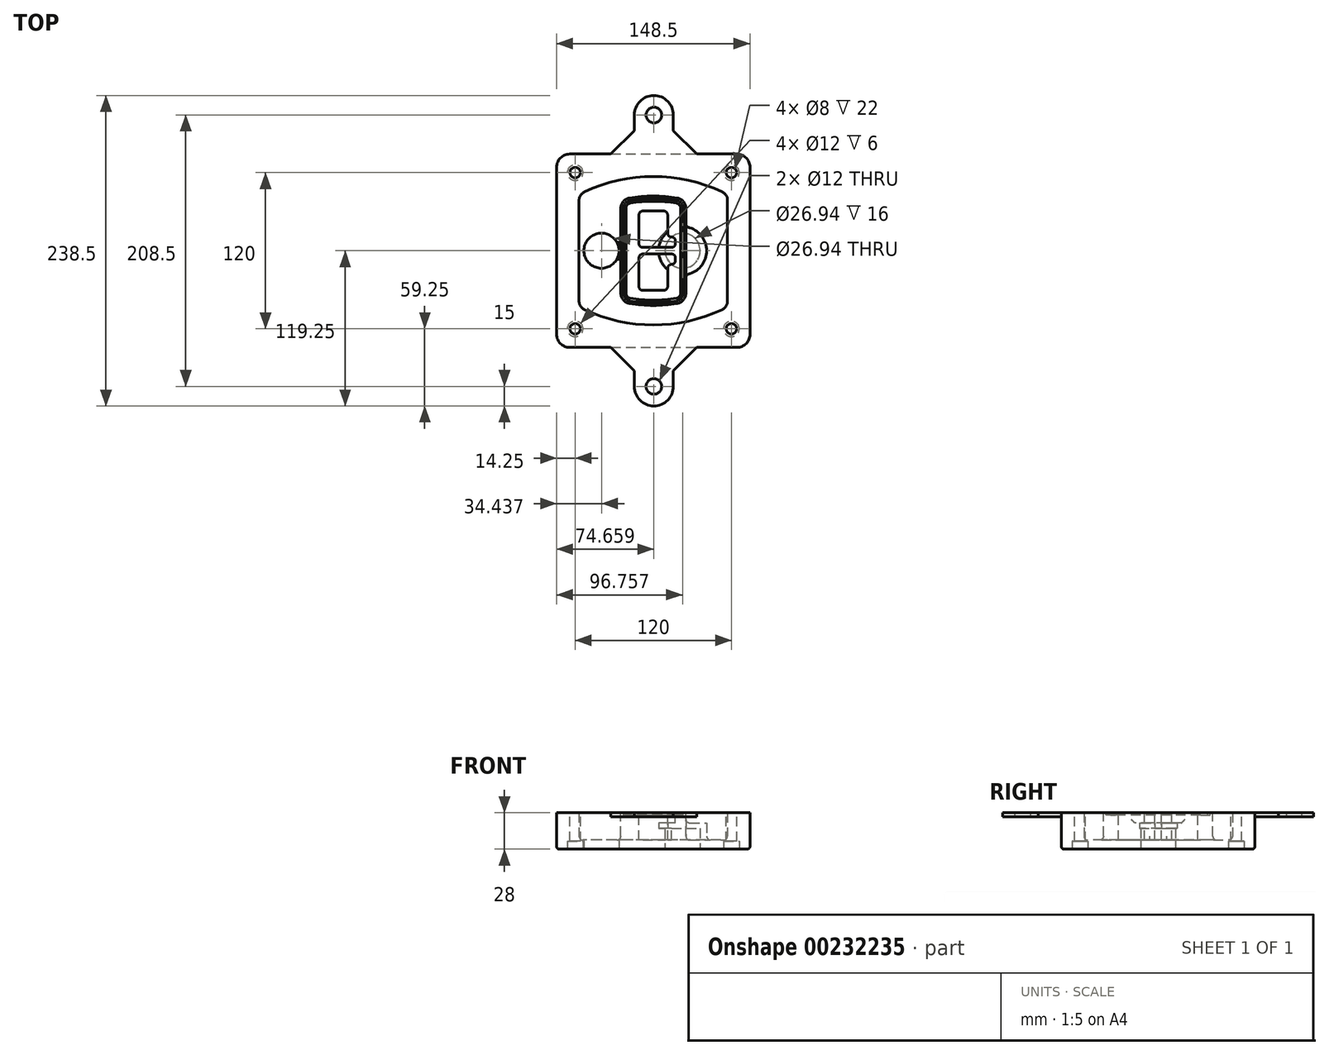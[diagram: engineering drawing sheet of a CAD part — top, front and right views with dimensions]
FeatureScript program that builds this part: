
annotation { "Feature Type Name" : "Feature", "Feature Type Description" : "" }
export const myFeature = defineFeature(function(context is Context, id is Id, definition is map)
    precondition{}
    {
        {
            var Q0;
            Q0=qCreatedBy(makeId("Top.planeOp"),FACE);
            var sketch = newSketch(context, id + "F0", { "sketchPlane" : qUnion([Q0])});
            skPoint(sketch, "E0.rect.middle", {"position": v(0, 0) * mm});
            skLineSegment(sketch, "E1.bottom", {"start": v(-64.25, -74.25) * mm, "end": v(64.25, -74.25) * mm});
            skLineSegment(sketch, "E1.top", {"start": v(-64.25, 74.25) * mm, "end": v(64.25, 74.25) * mm});
            skLineSegment(sketch, "E1.left", {"start": v(-74.25, -64.25) * mm, "end": v(-74.25, 64.25) * mm});
            skLineSegment(sketch, "E1.right", {"start": v(74.25, -64.25) * mm, "end": v(74.25, 64.25) * mm});
            skLineSegment(sketch, "E2", {"start": v(-74.25, 74.25) * mm, "end": v(74.25, -74.25) * mm, "construction": true});
            skLineSegment(sketch, "E3", {"start": v(74.25, 74.25) * mm, "end": v(-74.25, -74.25) * mm, "construction": true});
            skCircle(sketch, "E4", {"center": v(-60, 60) * mm, "radius": 4 * mm});
            skCircle(sketch, "E5", {"center": v(60, 60) * mm, "radius": 4 * mm});
            skCircle(sketch, "E6", {"center": v(60, -60) * mm, "radius": 4 * mm});
            skCircle(sketch, "E7", {"center": v(-60, -60) * mm, "radius": 4 * mm});
            skLineSegment(sketch, "E8", {"start": v(-60, 60) * mm, "end": v(60, 60) * mm, "construction": true});
            skLineSegment(sketch, "E9", {"start": v(60, 60) * mm, "end": v(60, -60) * mm, "construction": true});
            skLineSegment(sketch, "E10", {"start": v(60, -60) * mm, "end": v(-60, -60) * mm, "construction": true});
            skLineSegment(sketch, "E11", {"start": v(-60, -60) * mm, "end": v(-60, 60) * mm, "construction": true});
            skLineSegment(sketch, "E12", {"start": v(-60, 38.83) * mm, "end": v(-60, -38.83) * mm});
            skLineSegment(sketch, "E13", {"start": v(60, 38.83) * mm, "end": v(60, -38.83) * mm});
            skArc(sketch, "E14", {"start": v(54.26, 47.88) * mm, "mid": v(0, 60) * mm, "end": v(-54.26, 47.88) * mm});
            skArc(sketch, "E15", {"start": v(-54.26, -47.88) * mm, "mid": v(0, -60) * mm, "end": v(54.26, -47.88) * mm});
            skLineSegment(sketch, "E16", {"start": v(-60, 0) * mm, "end": v(60, 0) * mm, "construction": true});
            skPoint(sketch, "E17.visualSharp", {"position": v(-60, -45) * mm});
            skArc(sketch, "E17.filletArc", {"start": v(-60, -38.83) * mm, "mid": v(-58.44, -44.2) * mm, "end": v(-54.26, -47.88) * mm});
            skPoint(sketch, "E18.visualSharp", {"position": v(-60, 45) * mm});
            skArc(sketch, "E18.filletArc", {"start": v(-54.26, 47.88) * mm, "mid": v(-58.44, 44.2) * mm, "end": v(-60, 38.83) * mm});
            skPoint(sketch, "E19.visualSharp", {"position": v(60, 45) * mm});
            skArc(sketch, "E19.filletArc", {"start": v(60, 38.83) * mm, "mid": v(58.44, 44.2) * mm, "end": v(54.26, 47.88) * mm});
            skPoint(sketch, "E20.visualSharp", {"position": v(60, -45) * mm});
            skArc(sketch, "E20.filletArc", {"start": v(54.26, -47.88) * mm, "mid": v(58.44, -44.2) * mm, "end": v(60, -38.83) * mm});
            skPoint(sketch, "E21.visualSharp", {"position": v(-74.25, 74.25) * mm});
            skArc(sketch, "E21.filletArc", {"start": v(-64.25, 74.25) * mm, "mid": v(-71.32, 71.32) * mm, "end": v(-74.25, 64.25) * mm});
            skPoint(sketch, "E22.visualSharp", {"position": v(74.25, 74.25) * mm});
            skArc(sketch, "E22.filletArc", {"start": v(74.25, 64.25) * mm, "mid": v(71.32, 71.32) * mm, "end": v(64.25, 74.25) * mm});
            skPoint(sketch, "E23.visualSharp", {"position": v(74.25, -74.25) * mm});
            skArc(sketch, "E23.filletArc", {"start": v(64.25, -74.25) * mm, "mid": v(71.32, -71.32) * mm, "end": v(74.25, -64.25) * mm});
            skPoint(sketch, "E24.visualSharp", {"position": v(-74.25, -74.25) * mm});
            skArc(sketch, "E24.filletArc", {"start": v(-74.25, -64.25) * mm, "mid": v(-71.32, -71.32) * mm, "end": v(-64.25, -74.25) * mm});
            skArc(sketch, "E25.0", {"start": v(57, 38.83) * mm, "mid": v(55.9, 42.58) * mm, "end": v(52.98, 45.17) * mm});
            skLineSegment(sketch, "E25.1", {"start": v(57, 38.83) * mm, "end": v(57, -38.83) * mm});
            skArc(sketch, "E25.2", {"start": v(52.98, -45.17) * mm, "mid": v(55.9, -42.58) * mm, "end": v(57, -38.83) * mm});
            skArc(sketch, "E25.3", {"start": v(-52.98, -45.17) * mm, "mid": v(0, -57) * mm, "end": v(52.98, -45.17) * mm});
            skArc(sketch, "E25.4", {"start": v(-57, -38.83) * mm, "mid": v(-55.9, -42.58) * mm, "end": v(-52.98, -45.17) * mm});
            skArc(sketch, "E25.5", {"start": v(52.98, 45.17) * mm, "mid": v(0, 57) * mm, "end": v(-52.98, 45.17) * mm});
            skLineSegment(sketch, "E25.6", {"start": v(-57, 38.83) * mm, "end": v(-57, -38.83) * mm});
            skArc(sketch, "E25.7", {"start": v(-52.98, 45.17) * mm, "mid": v(-55.9, 42.58) * mm, "end": v(-57, 38.83) * mm});
            skArc(sketch, "E26.0", {"start": v(-55.96, 51.5) * mm, "mid": v(-61.82, 46.33) * mm, "end": v(-64, 38.83) * mm});
            skArc(sketch, "E26.1", {"start": v(55.96, 51.5) * mm, "mid": v(0, 64) * mm, "end": v(-55.96, 51.5) * mm});
            skArc(sketch, "E26.2", {"start": v(64, 38.83) * mm, "mid": v(61.82, 46.33) * mm, "end": v(55.96, 51.5) * mm});
            skLineSegment(sketch, "E26.3", {"start": v(64, 38.83) * mm, "end": v(64, -38.83) * mm});
            skArc(sketch, "E26.4", {"start": v(55.96, -51.5) * mm, "mid": v(61.82, -46.33) * mm, "end": v(64, -38.83) * mm});
            skLineSegment(sketch, "E26.5", {"start": v(-64, 38.83) * mm, "end": v(-64, -38.83) * mm});
            skArc(sketch, "E26.6", {"start": v(-55.96, -51.5) * mm, "mid": v(0, -64) * mm, "end": v(55.96, -51.5) * mm});
            skArc(sketch, "E26.7", {"start": v(-64, -38.83) * mm, "mid": v(-61.82, -46.33) * mm, "end": v(-55.96, -51.5) * mm});
            skSolve(sketch);
        }
        {
            var Q0;
            Q0=makeQuery(id+"F0.imprint","IMPRINT",FACE,{"disambiguationData":[TD([[makeQuery(id+"F0.imprint","IMPRINT",EDGE,{"derivedFrom":sQuery(id+"F0.wireOp",EDGE,"E1.bottom")}),1.0]])]});
            var Q1;
            Q1=makeQuery(id+"F0.imprint","IMPRINT",FACE,{"disambiguationData":[TD([[makeQuery(id+"F0.imprint","IMPRINT",EDGE,{"derivedFrom":sQuery(id+"F0.wireOp",EDGE,"E12")}),1.0]])]});
            var Q2;
            Q2=makeQuery(id+"F0.imprint","IMPRINT",FACE,{"disambiguationData":[TD([[makeQuery(id+"F0.imprint","IMPRINT",EDGE,{"derivedFrom":sQuery(id+"F0.wireOp",EDGE,"E25.0")}),1.0]])]});
            var Q3;
            Q3=makeQuery(id+"F0.imprint","IMPRINT",FACE,{"disambiguationData":[TD([[makeQuery(id+"F0.imprint","IMPRINT",EDGE,{"derivedFrom":sQuery(id+"F0.wireOp",EDGE,"E12")}),-1.0]])]});
            extrude(context, id + "F1", {"entities" : qUnion([Q0, Q1, Q2, Q3]), "oppositeDirection" : true, "depth" : 25 * mm});
        }
        {
            var Q0;
            Q0=makeQuery(id+"F0.imprint","IMPRINT",FACE,{"disambiguationData":[TD([[makeQuery(id+"F0.imprint","IMPRINT",EDGE,{"derivedFrom":sQuery(id+"F0.wireOp",EDGE,"E12")}),1.0]])]});
            extrude(context, id + "F2", {"entities" : qUnion([Q0]), "operationType" : NewBodyOperationType.ADD, "depth" : 3 * mm});
        }
        {
            var Q0;
            Q0=makeQuery(id+"F0.imprint","IMPRINT",FACE,{"disambiguationData":[TD([[makeQuery(id+"F0.imprint","IMPRINT",EDGE,{"derivedFrom":sQuery(id+"F0.wireOp",EDGE,"E25.0")}),1.0]])]});
            extrude(context, id + "F3", {"entities" : qUnion([Q0]), "operationType" : NewBodyOperationType.REMOVE, "oppositeDirection" : true, "depth" : 18 * mm});
        }
        {
            var Q0;
            Q0=makeQuery(id+"F2.opExtrude","CAP_FACE",FACE,{"disambiguationData":[OSD([sQuery(id+"F0.wireOp",EDGE,"E12"),sQuery(id+"F0.wireOp",EDGE,"E13"),sQuery(id+"F0.wireOp",EDGE,"E14"),sQuery(id+"F0.wireOp",EDGE,"E15"),sQuery(id+"F0.wireOp",EDGE,"E17.filletArc"),sQuery(id+"F0.wireOp",EDGE,"E18.filletArc"),sQuery(id+"F0.wireOp",EDGE,"E19.filletArc"),sQuery(id+"F0.wireOp",EDGE,"E20.filletArc"),sQuery(id+"F0.wireOp",EDGE,"E25.0"),sQuery(id+"F0.wireOp",EDGE,"E25.1"),sQuery(id+"F0.wireOp",EDGE,"E25.2"),sQuery(id+"F0.wireOp",EDGE,"E25.3"),sQuery(id+"F0.wireOp",EDGE,"E25.4"),sQuery(id+"F0.wireOp",EDGE,"E25.5"),sQuery(id+"F0.wireOp",EDGE,"E25.6"),sQuery(id+"F0.wireOp",EDGE,"E25.7")])],"isStart":false});
            var sketch = newSketch(context, id + "F4", { "sketchPlane" : qUnion([Q0])});
            skArc(sketch, "E27.0", {"start": v(-18.34, -40.45) * mm, "mid": v(0, -42) * mm, "end": v(18.34, -40.45) * mm});
            skArc(sketch, "E28.0", {"start": v(18.34, 40.45) * mm, "mid": v(0, 42) * mm, "end": v(-18.34, 40.45) * mm});
            skLineSegment(sketch, "E29", {"start": v(-25, 32.57) * mm, "end": v(-25, -32.57) * mm});
            skLineSegment(sketch, "E30", {"start": v(25, 32.57) * mm, "end": v(25, -32.57) * mm});
            skLineSegment(sketch, "E31", {"start": v(-25, 39.1) * mm, "end": v(25, 39.1) * mm, "construction": true});
            skLineSegment(sketch, "E32", {"start": v(-25, -39.1) * mm, "end": v(25, -39.1) * mm, "construction": true});
            skPoint(sketch, "E33.visualSharp", {"position": v(-25, 39.1) * mm});
            skArc(sketch, "E33.filletArc", {"start": v(-18.34, 40.45) * mm, "mid": v(-23.11, 37.73) * mm, "end": v(-25, 32.57) * mm});
            skPoint(sketch, "E34.visualSharp", {"position": v(25, 39.1) * mm});
            skArc(sketch, "E34.filletArc", {"start": v(25, 32.57) * mm, "mid": v(23.11, 37.73) * mm, "end": v(18.34, 40.45) * mm});
            skPoint(sketch, "E35.visualSharp", {"position": v(25, -39.1) * mm});
            skArc(sketch, "E35.filletArc", {"start": v(18.34, -40.45) * mm, "mid": v(23.11, -37.73) * mm, "end": v(25, -32.57) * mm});
            skPoint(sketch, "E36.visualSharp", {"position": v(-25, -39.1) * mm});
            skArc(sketch, "E36.filletArc", {"start": v(-25, -32.57) * mm, "mid": v(-23.11, -37.73) * mm, "end": v(-18.34, -40.45) * mm});
            skArc(sketch, "E37.0", {"start": v(52.98, 45.17) * mm, "mid": v(0, 57) * mm, "end": v(-52.98, 45.17) * mm});
            skArc(sketch, "E37.1", {"start": v(-52.98, 45.17) * mm, "mid": v(-55.9, 42.58) * mm, "end": v(-57, 38.83) * mm});
            skLineSegment(sketch, "E37.2", {"start": v(-57, 38.83) * mm, "end": v(-57, -38.83) * mm});
            skArc(sketch, "E37.3", {"start": v(-57, -38.83) * mm, "mid": v(-55.9, -42.58) * mm, "end": v(-52.98, -45.17) * mm});
            skArc(sketch, "E37.4", {"start": v(-52.98, -45.17) * mm, "mid": v(0, -57) * mm, "end": v(52.98, -45.17) * mm});
            skArc(sketch, "E37.5", {"start": v(52.98, -45.17) * mm, "mid": v(55.9, -42.58) * mm, "end": v(57, -38.83) * mm});
            skLineSegment(sketch, "E37.6", {"start": v(57, 38.83) * mm, "end": v(57, -38.83) * mm});
            skArc(sketch, "E37.7", {"start": v(57, 38.83) * mm, "mid": v(55.9, 42.58) * mm, "end": v(52.98, 45.17) * mm});
            skLineSegment(sketch, "E38.0", {"start": v(23, 32.57) * mm, "end": v(23, -32.57) * mm});
            skArc(sketch, "E38.1", {"start": v(18, -38.48) * mm, "mid": v(21.58, -36.44) * mm, "end": v(23, -32.57) * mm});
            skArc(sketch, "E38.2", {"start": v(-18, -38.48) * mm, "mid": v(0, -40) * mm, "end": v(18, -38.48) * mm});
            skArc(sketch, "E38.3", {"start": v(-23, -32.57) * mm, "mid": v(-21.58, -36.44) * mm, "end": v(-18, -38.48) * mm});
            skLineSegment(sketch, "E38.4", {"start": v(-23, 32.57) * mm, "end": v(-23, -32.57) * mm});
            skArc(sketch, "E38.5", {"start": v(23, 32.57) * mm, "mid": v(21.58, 36.44) * mm, "end": v(18, 38.48) * mm});
            skArc(sketch, "E38.6", {"start": v(-18, 38.48) * mm, "mid": v(-21.58, 36.44) * mm, "end": v(-23, 32.57) * mm});
            skArc(sketch, "E38.7", {"start": v(18, 38.48) * mm, "mid": v(0, 40) * mm, "end": v(-18, 38.48) * mm});
            skArc(sketch, "E39.0", {"start": v(21, 32.57) * mm, "mid": v(20.06, 35.15) * mm, "end": v(17.67, 36.5) * mm});
            skLineSegment(sketch, "E39.1", {"start": v(21, 32.57) * mm, "end": v(21, -32.57) * mm});
            skArc(sketch, "E39.2", {"start": v(17.67, -36.5) * mm, "mid": v(20.06, -35.15) * mm, "end": v(21, -32.57) * mm});
            skArc(sketch, "E39.3", {"start": v(-17.67, -36.5) * mm, "mid": v(0, -38) * mm, "end": v(17.67, -36.5) * mm});
            skArc(sketch, "E39.4", {"start": v(-21, -32.57) * mm, "mid": v(-20.06, -35.15) * mm, "end": v(-17.67, -36.5) * mm});
            skArc(sketch, "E39.5", {"start": v(17.67, 36.5) * mm, "mid": v(0, 38) * mm, "end": v(-17.67, 36.5) * mm});
            skLineSegment(sketch, "E39.6", {"start": v(-21, 32.57) * mm, "end": v(-21, -32.57) * mm});
            skArc(sketch, "E39.7", {"start": v(-17.67, 36.5) * mm, "mid": v(-20.06, 35.15) * mm, "end": v(-21, 32.57) * mm});
            skLineSegment(sketch, "E40", {"start": v(-25, 0) * mm, "end": v(25, 0) * mm, "construction": true});
            skLineSegment(sketch, "E41", {"start": v(-11, 5.5) * mm, "end": v(-11, 27.5) * mm});
            skLineSegment(sketch, "E42", {"start": v(-8, 30.5) * mm, "end": v(8, 30.5) * mm});
            skLineSegment(sketch, "E43", {"start": v(11, 27.5) * mm, "end": v(11, 13.5) * mm});
            skLineSegment(sketch, "E44", {"start": v(14, 10.5) * mm, "end": v(14, 10.5) * mm});
            skLineSegment(sketch, "E45", {"start": v(17, 7.5) * mm, "end": v(17, 5.5) * mm});
            skLineSegment(sketch, "E46", {"start": v(14, 2.5) * mm, "end": v(-8, 2.5) * mm});
            skPoint(sketch, "E47.visualSharp", {"position": v(-11, 30.5) * mm});
            skArc(sketch, "E47.filletArc", {"start": v(-8, 30.5) * mm, "mid": v(-10.12, 29.62) * mm, "end": v(-11, 27.5) * mm});
            skPoint(sketch, "E48.visualSharp", {"position": v(11, 30.5) * mm});
            skArc(sketch, "E48.filletArc", {"start": v(11, 27.5) * mm, "mid": v(10.12, 29.62) * mm, "end": v(8, 30.5) * mm});
            skPoint(sketch, "E49.visualSharp", {"position": v(11, 10.5) * mm});
            skArc(sketch, "E49.filletArc", {"start": v(11, 13.5) * mm, "mid": v(11.88, 11.38) * mm, "end": v(14, 10.5) * mm});
            skPoint(sketch, "E50.visualSharp", {"position": v(17, 10.5) * mm});
            skArc(sketch, "E50.filletArc", {"start": v(17, 7.5) * mm, "mid": v(16.12, 9.62) * mm, "end": v(14, 10.5) * mm});
            skPoint(sketch, "E51.visualSharp", {"position": v(17, 2.5) * mm});
            skArc(sketch, "E51.filletArc", {"start": v(14, 2.5) * mm, "mid": v(16.12, 3.38) * mm, "end": v(17, 5.5) * mm});
            skPoint(sketch, "E52.visualSharp", {"position": v(-11, 2.5) * mm});
            skArc(sketch, "E52.filletArc", {"start": v(-11, 5.5) * mm, "mid": v(-10.12, 3.38) * mm, "end": v(-8, 2.5) * mm});
            skLineSegment(sketch, "E53.0.MirrorCS", {"start": v(14, -2.5) * mm, "end": v(-8, -2.5) * mm});
            skArc(sketch, "E54.0.MirrorCS", {"start": v(-11, -5.5) * mm, "mid": v(-10.12, -3.38) * mm, "end": v(-8, -2.5) * mm});
            skLineSegment(sketch, "E55.0.MirrorCS", {"start": v(-11, -5.5) * mm, "end": v(-11, -27.5) * mm});
            skArc(sketch, "E56.0.MirrorCS", {"start": v(-8, -30.5) * mm, "mid": v(-10.12, -29.62) * mm, "end": v(-11, -27.5) * mm});
            skLineSegment(sketch, "E57.0.MirrorCS", {"start": v(-8, -30.5) * mm, "end": v(8, -30.5) * mm});
            skArc(sketch, "E58.0.MirrorCS", {"start": v(11, -27.5) * mm, "mid": v(10.12, -29.62) * mm, "end": v(8, -30.5) * mm});
            skLineSegment(sketch, "E59.0.MirrorCS", {"start": v(11, -27.5) * mm, "end": v(11, -13.5) * mm});
            skArc(sketch, "E60.0.MirrorCS", {"start": v(11, -13.5) * mm, "mid": v(11.88, -11.38) * mm, "end": v(14, -10.5) * mm});
            skArc(sketch, "E61.0.MirrorCS", {"start": v(17, -7.5) * mm, "mid": v(16.12, -9.62) * mm, "end": v(14, -10.5) * mm});
            skLineSegment(sketch, "E62.0.MirrorCS", {"start": v(17, -7.5) * mm, "end": v(17, -5.5) * mm});
            skArc(sketch, "E63.0.MirrorCS", {"start": v(14, -2.5) * mm, "mid": v(16.12, -3.38) * mm, "end": v(17, -5.5) * mm});
            skSolve(sketch);
        }
        {
            var Q0;
            Q0=makeQuery(id+"F4.imprint","IMPRINT",FACE,{"disambiguationData":[TD([[makeQuery(id+"F4.imprint","IMPRINT",EDGE,{"derivedFrom":sQuery(id+"F4.wireOp",EDGE,"E27.0")}),1.0]])]});
            var Q1;
            Q1=makeQuery(id+"F4.imprint","IMPRINT",FACE,{"disambiguationData":[TD([[makeQuery(id+"F4.imprint","IMPRINT",EDGE,{"derivedFrom":sQuery(id+"F4.wireOp",EDGE,"E38.0")}),-1.0]])]});
            var Q2;
            Q2=makeQuery(id+"F4.imprint","IMPRINT",FACE,{"disambiguationData":[TD([[makeQuery(id+"F4.imprint","IMPRINT",EDGE,{"derivedFrom":sQuery(id+"F4.wireOp",EDGE,"E39.0")}),1.0]])]});
            extrude(context, id + "F5", {"entities" : qUnion([Q0, Q1, Q2]), "operationType" : NewBodyOperationType.ADD, "endBound" : BoundingType.UP_TO_NEXT, "oppositeDirection" : true, "depth" : 25 * mm});
        }
        {
            var Q0;
            Q0=makeQuery(id+"F4.imprint","IMPRINT",FACE,{"disambiguationData":[TD([[makeQuery(id+"F4.imprint","IMPRINT",EDGE,{"derivedFrom":sQuery(id+"F4.wireOp",EDGE,"E38.0")}),-1.0]])]});
            extrude(context, id + "F6", {"entities" : qUnion([Q0]), "operationType" : NewBodyOperationType.REMOVE, "oppositeDirection" : true, "depth" : 2 * mm});
        }
        {
            var Q0;
            Q0=makeQuery(id+"F1.opExtrude","CAP_FACE",FACE,{"disambiguationData":[OSD([sQuery(id+"F0.wireOp",EDGE,"E1.bottom"),sQuery(id+"F0.wireOp",EDGE,"E1.top"),sQuery(id+"F0.wireOp",EDGE,"E1.left"),sQuery(id+"F0.wireOp",EDGE,"E1.right"),sQuery(id+"F0.wireOp",EDGE,"E4"),sQuery(id+"F0.wireOp",EDGE,"E5"),sQuery(id+"F0.wireOp",EDGE,"E6"),sQuery(id+"F0.wireOp",EDGE,"E7"),sQuery(id+"F0.wireOp",EDGE,"E21.filletArc"),sQuery(id+"F0.wireOp",EDGE,"E22.filletArc"),sQuery(id+"F0.wireOp",EDGE,"E23.filletArc"),sQuery(id+"F0.wireOp",EDGE,"E24.filletArc")])],"isStart":false});
            var sketch = newSketch(context, id + "F7", { "sketchPlane" : qUnion([Q0])});
            skCircle(sketch, "E64", {"center": v(22.5, 0) * mm, "radius": 13.47 * mm});
            skCircle(sketch, "E65", {"center": v(-39.81, 0) * mm, "radius": 13.47 * mm});
            skLineSegment(sketch, "E66", {"start": v(74.25, 0) * mm, "end": v(-74.25, 0) * mm});
            skCircle(sketch, "E67", {"center": v(22.5, 0) * mm, "radius": 18.47 * mm});
            skCircle(sketch, "E68", {"center": v(60, -60) * mm, "radius": 6 * mm});
            skCircle(sketch, "E69", {"center": v(-60, -60) * mm, "radius": 6 * mm});
            skCircle(sketch, "E70", {"center": v(-60, 60) * mm, "radius": 6 * mm});
            skCircle(sketch, "E71", {"center": v(60, 60) * mm, "radius": 6 * mm});
            skSolve(sketch);
        }
        {
            var Q0;
            {var subQ1=sQuery(id+"F7.wireOp",EDGE,"E66");var subQ4=sQuery(id+"F7.wireOp",EDGE,"E64");var subQ6=makeQuery(id+"F7.imprint","INTERSECT",VERTEX,{"disambiguationData":[OD(0.0)],"derivedFrom":[subQ4,subQ1]});Q0=makeQuery(id+"F7.imprint","IMPRINT",FACE,{"disambiguationData":[TD([[makeQuery(id+"F7.imprint","IMPRINT",EDGE,{"disambiguationData":[TD([[subQ6,-1.0]])],"derivedFrom":subQ4}),-1.0]])]});}
            var Q1;
            {var subQ0=sQuery(id+"F7.wireOp",EDGE,"E66");var subQ1=sQuery(id+"F7.wireOp",EDGE,"E64");var subQ3=makeQuery(id+"F7.imprint","INTERSECT",VERTEX,{"disambiguationData":[OD(0.0)],"derivedFrom":[subQ1,subQ0]});Q1=makeQuery(id+"F7.imprint","IMPRINT",FACE,{"disambiguationData":[TD([[makeQuery(id+"F7.imprint","IMPRINT",EDGE,{"disambiguationData":[TD([[subQ3,-1.0]])],"derivedFrom":subQ1}),1.0]])]});}
            var Q2;
            {var subQ0=sQuery(id+"F7.wireOp",EDGE,"E66");var subQ1=sQuery(id+"F7.wireOp",EDGE,"E64");var subQ3=makeQuery(id+"F7.imprint","INTERSECT",VERTEX,{"disambiguationData":[OD(0.0)],"derivedFrom":[subQ1,subQ0]});Q2=makeQuery(id+"F7.imprint","IMPRINT",FACE,{"disambiguationData":[TD([[makeQuery(id+"F7.imprint","IMPRINT",EDGE,{"disambiguationData":[TD([[subQ3,1.0]])],"derivedFrom":subQ1}),1.0]])]});}
            var Q3;
            {var subQ1=sQuery(id+"F7.wireOp",EDGE,"E66");var subQ4=sQuery(id+"F7.wireOp",EDGE,"E64");var subQ6=makeQuery(id+"F7.imprint","INTERSECT",VERTEX,{"disambiguationData":[OD(0.0)],"derivedFrom":[subQ4,subQ1]});Q3=makeQuery(id+"F7.imprint","IMPRINT",FACE,{"disambiguationData":[TD([[makeQuery(id+"F7.imprint","IMPRINT",EDGE,{"disambiguationData":[TD([[subQ6,1.0]])],"derivedFrom":subQ4}),-1.0]])]});}
            extrude(context, id + "F8", {"entities" : qUnion([Q0, Q1, Q2, Q3]), "operationType" : NewBodyOperationType.ADD, "oppositeDirection" : true, "depth" : 20 * mm});
        }
        {
            var Q0;
            {var subQ0=sQuery(id+"F7.wireOp",EDGE,"E66");var subQ1=sQuery(id+"F7.wireOp",EDGE,"E64");var subQ3=makeQuery(id+"F7.imprint","INTERSECT",VERTEX,{"disambiguationData":[OD(0.0)],"derivedFrom":[subQ1,subQ0]});Q0=makeQuery(id+"F7.imprint","IMPRINT",FACE,{"disambiguationData":[TD([[makeQuery(id+"F7.imprint","IMPRINT",EDGE,{"disambiguationData":[TD([[subQ3,-1.0]])],"derivedFrom":subQ1}),1.0]])]});}
            var Q1;
            {var subQ0=sQuery(id+"F7.wireOp",EDGE,"E66");var subQ1=sQuery(id+"F7.wireOp",EDGE,"E64");var subQ3=makeQuery(id+"F7.imprint","INTERSECT",VERTEX,{"disambiguationData":[OD(0.0)],"derivedFrom":[subQ1,subQ0]});Q1=makeQuery(id+"F7.imprint","IMPRINT",FACE,{"disambiguationData":[TD([[makeQuery(id+"F7.imprint","IMPRINT",EDGE,{"disambiguationData":[TD([[subQ3,1.0]])],"derivedFrom":subQ1}),1.0]])]});}
            extrude(context, id + "F9", {"entities" : qUnion([Q0, Q1]), "operationType" : NewBodyOperationType.REMOVE, "oppositeDirection" : true, "depth" : 16 * mm});
        }
        {
            var Q0;
            {var subQ0=sQuery(id+"F7.wireOp",EDGE,"E66");var subQ1=sQuery(id+"F7.wireOp",EDGE,"E65");var subQ3=makeQuery(id+"F7.imprint","INTERSECT",VERTEX,{"disambiguationData":[OD(0.0)],"derivedFrom":[subQ1,subQ0]});Q0=makeQuery(id+"F7.imprint","IMPRINT",FACE,{"disambiguationData":[TD([[makeQuery(id+"F7.imprint","IMPRINT",EDGE,{"disambiguationData":[TD([[subQ3,-1.0]])],"derivedFrom":subQ1}),1.0]])]});}
            var Q1;
            {var subQ0=sQuery(id+"F7.wireOp",EDGE,"E66");var subQ1=sQuery(id+"F7.wireOp",EDGE,"E65");var subQ3=makeQuery(id+"F7.imprint","INTERSECT",VERTEX,{"disambiguationData":[OD(0.0)],"derivedFrom":[subQ1,subQ0]});Q1=makeQuery(id+"F7.imprint","IMPRINT",FACE,{"disambiguationData":[TD([[makeQuery(id+"F7.imprint","IMPRINT",EDGE,{"disambiguationData":[TD([[subQ3,1.0]])],"derivedFrom":subQ1}),1.0]])]});}
            extrude(context, id + "F10", {"entities" : qUnion([Q0, Q1]), "operationType" : NewBodyOperationType.REMOVE, "oppositeDirection" : true, "depth" : 25 * mm});
        }
        {
            var Q0;
            Q0=makeQuery(id+"F7.imprint","IMPRINT",FACE,{"disambiguationData":[TD([[makeQuery(id+"F7.imprint","IMPRINT",EDGE,{"derivedFrom":sQuery(id+"F7.wireOp",EDGE,"E68")}),1.0]])]});
            var Q1;
            Q1=makeQuery(id+"F7.imprint","IMPRINT",FACE,{"disambiguationData":[TD([[makeQuery(id+"F7.imprint","IMPRINT",EDGE,{"derivedFrom":makeQuery(id+"F1.opExtrude","CAP_EDGE",EDGE,{"disambiguationData":[OSD([sQuery(id+"F0.wireOp",EDGE,"E5")])],"isStart":false})}),-1.0]])]});
            var Q2;
            Q2=makeQuery(id+"F7.imprint","IMPRINT",FACE,{"disambiguationData":[TD([[makeQuery(id+"F7.imprint","IMPRINT",EDGE,{"derivedFrom":sQuery(id+"F7.wireOp",EDGE,"E69")}),1.0]])]});
            var Q3;
            Q3=makeQuery(id+"F7.imprint","IMPRINT",FACE,{"disambiguationData":[TD([[makeQuery(id+"F7.imprint","IMPRINT",EDGE,{"derivedFrom":makeQuery(id+"F1.opExtrude","CAP_EDGE",EDGE,{"disambiguationData":[OSD([sQuery(id+"F0.wireOp",EDGE,"E4")])],"isStart":false})}),-1.0]])]});
            var Q4;
            Q4=makeQuery(id+"F7.imprint","IMPRINT",FACE,{"disambiguationData":[TD([[makeQuery(id+"F7.imprint","IMPRINT",EDGE,{"derivedFrom":sQuery(id+"F7.wireOp",EDGE,"E70")}),1.0]])]});
            var Q5;
            Q5=makeQuery(id+"F7.imprint","IMPRINT",FACE,{"disambiguationData":[TD([[makeQuery(id+"F7.imprint","IMPRINT",EDGE,{"derivedFrom":makeQuery(id+"F1.opExtrude","CAP_EDGE",EDGE,{"disambiguationData":[OSD([sQuery(id+"F0.wireOp",EDGE,"E7")])],"isStart":false})}),-1.0]])]});
            var Q6;
            Q6=makeQuery(id+"F7.imprint","IMPRINT",FACE,{"disambiguationData":[TD([[makeQuery(id+"F7.imprint","IMPRINT",EDGE,{"derivedFrom":sQuery(id+"F7.wireOp",EDGE,"E71")}),1.0]])]});
            var Q7;
            Q7=makeQuery(id+"F7.imprint","IMPRINT",FACE,{"disambiguationData":[TD([[makeQuery(id+"F7.imprint","IMPRINT",EDGE,{"derivedFrom":makeQuery(id+"F1.opExtrude","CAP_EDGE",EDGE,{"disambiguationData":[OSD([sQuery(id+"F0.wireOp",EDGE,"E6")])],"isStart":false})}),-1.0]])]});
            extrude(context, id + "F11", {"entities" : qUnion([Q0, Q1, Q2, Q3, Q4, Q5, Q6, Q7]), "operationType" : NewBodyOperationType.REMOVE, "oppositeDirection" : true, "depth" : 6 * mm});
        }
        {
            var Q0;
            Q0=makeQuery(id+"F9.boolean.opBoolean","COPY",FACE,{"derivedFrom":makeQuery(id+"F9.opExtrude","CAP_FACE",FACE,{"disambiguationData":[OSD([sQuery(id+"F7.wireOp",EDGE,"E64")])],"isStart":false})});
            var sketch = newSketch(context, id + "F12", { "sketchPlane" : qUnion([Q0])});
            skArc(sketch, "E72.0", {"start": v(11, 14.45) * mm, "mid": v(6.45, 9.13) * mm, "end": v(4.2, 2.5) * mm});
            skArc(sketch, "E72.1", {"start": v(4.2, -2.5) * mm, "mid": v(6.45, -9.13) * mm, "end": v(11, -14.45) * mm});
            skLineSegment(sketch, "E73", {"start": v(4.2, -2.5) * mm, "end": v(14, -2.5) * mm});
            skLineSegment(sketch, "E74.0", {"start": v(14, 2.5) * mm, "end": v(4.2, 2.5) * mm});
            skArc(sketch, "E74.1", {"start": v(14, 2.5) * mm, "mid": v(16.12, 3.38) * mm, "end": v(17, 5.5) * mm});
            skLineSegment(sketch, "E74.2", {"start": v(17, 7.5) * mm, "end": v(17, 5.5) * mm});
            skArc(sketch, "E74.3", {"start": v(17, 7.5) * mm, "mid": v(16.12, 9.62) * mm, "end": v(14, 10.5) * mm});
            skArc(sketch, "E74.4", {"start": v(11, 13.5) * mm, "mid": v(11.88, 11.38) * mm, "end": v(14, 10.5) * mm});
            skLineSegment(sketch, "E74.5", {"start": v(11, 14.45) * mm, "end": v(11, 13.5) * mm});
            skLineSegment(sketch, "E74.7", {"start": v(14, -2.5) * mm, "end": v(4.2, -2.5) * mm});
            skArc(sketch, "E74.8", {"start": v(14, -2.5) * mm, "mid": v(16.12, -3.38) * mm, "end": v(17, -5.5) * mm});
            skLineSegment(sketch, "E74.9", {"start": v(17, -7.5) * mm, "end": v(17, -5.5) * mm});
            skArc(sketch, "E74.10", {"start": v(17, -7.5) * mm, "mid": v(16.12, -9.62) * mm, "end": v(14, -10.5) * mm});
            skArc(sketch, "E74.11", {"start": v(11, -13.5) * mm, "mid": v(11.88, -11.38) * mm, "end": v(14, -10.5) * mm});
            skLineSegment(sketch, "E74.12", {"start": v(11, -14.45) * mm, "end": v(11, -13.5) * mm});
            skPoint(sketch, "E75.orphan", {"position": v(11, -27.5) * mm});
            skPoint(sketch, "E76.orphan", {"position": v(-8, -2.5) * mm});
            skPoint(sketch, "E77.orphan", {"position": v(-8, 2.5) * mm});
            skPoint(sketch, "E78.orphan", {"position": v(11, 27.5) * mm});
            skSolve(sketch);
        }
        {
            var Q0;
            {var subQ7=sQuery(id+"F12.wireOp",EDGE,"E72.0");var subQ14=sQuery(id+"F12.wireOp",EDGE,"E72.1");var subQ16=sQuery(id+"F12.wireOp",EDGE,"E74.1");var subQ18=sQuery(id+"F12.wireOp",EDGE,"E74.8");Q0=qUnion([makeQuery(id+"F12.imprint","IMPRINT",FACE,{"disambiguationData":[TD([[makeQuery(id+"F12.imprint","IMPRINT",EDGE,{"derivedFrom":subQ7}),1.0]])]}),makeQuery(id+"F12.imprint","IMPRINT",FACE,{"disambiguationData":[TD([[makeQuery(id+"F12.imprint","IMPRINT",EDGE,{"derivedFrom":subQ14}),1.0]])]}),makeQuery(id+"F12.imprint","IMPRINT",FACE,{"disambiguationData":[TD([[makeQuery(id+"F12.imprint","IMPRINT",EDGE,{"derivedFrom":subQ16}),1.0]])]}),makeQuery(id+"F12.imprint","IMPRINT",FACE,{"disambiguationData":[TD([[makeQuery(id+"F12.imprint","IMPRINT",EDGE,{"derivedFrom":subQ18}),-1.0]])]})]);}
            var Q1;
            Q1=makeQuery(id+"F5.boolean.opBoolean","SPLIT",FACE,{"disambiguationData":[TD([makeQuery(id+"F5.opExtrude","SWEPT_FACE",FACE,{"disambiguationData":[OSD([sQuery(id+"F4.wireOp",EDGE,"E41")])]})])],"derivedFrom":makeQuery(id+"F3.boolean.opBoolean","COPY",FACE,{"derivedFrom":makeQuery(id+"F3.opExtrude","CAP_FACE",FACE,{"disambiguationData":[OSD([sQuery(id+"F0.wireOp",EDGE,"E25.0"),sQuery(id+"F0.wireOp",EDGE,"E25.1"),sQuery(id+"F0.wireOp",EDGE,"E25.2"),sQuery(id+"F0.wireOp",EDGE,"E25.3"),sQuery(id+"F0.wireOp",EDGE,"E25.4"),sQuery(id+"F0.wireOp",EDGE,"E25.5"),sQuery(id+"F0.wireOp",EDGE,"E25.6"),sQuery(id+"F0.wireOp",EDGE,"E25.7")])],"isStart":false})})});
            extrude(context, id + "F13", {"entities" : qUnion([Q0]), "operationType" : NewBodyOperationType.REMOVE, "endBound" : BoundingType.UP_TO_SURFACE, "endBoundEntityFace" : qUnion([Q1]), "depth" : 25 * mm});
        }
        {
            var Q0;
            Q0=makeQuery(id+"F3.boolean.opBoolean","COPY",EDGE,{"derivedFrom":makeQuery(id+"F3.opExtrude","CAP_EDGE",EDGE,{"disambiguationData":[OSD([sQuery(id+"F0.wireOp",EDGE,"E25.6")])],"isStart":false})});
            var Q1;
            Q1=makeQuery(id+"F8.boolean.opBoolean","INTERSECT",EDGE,{"derivedFrom":[makeQuery(id+"F5.opExtrude","SWEPT_FACE",FACE,{"disambiguationData":[OSD([sQuery(id+"F4.wireOp",EDGE,"E30")])]}),makeQuery(id+"F8.opExtrude","CAP_FACE",FACE,{"disambiguationData":[OSD([sQuery(id+"F7.wireOp",EDGE,"E67")])],"isStart":false})]});
            var Q2;
            Q2=makeQuery(id+"F8.boolean.opBoolean","INTERSECT",EDGE,{"disambiguationData":[OD(1.0)],"derivedFrom":[makeQuery(id+"F5.opExtrude","SWEPT_FACE",FACE,{"disambiguationData":[OSD([sQuery(id+"F4.wireOp",EDGE,"E30")])]}),makeQuery(id+"F8.opExtrude","SWEPT_FACE",FACE,{"disambiguationData":[OSD([sQuery(id+"F7.wireOp",EDGE,"E67")])]})]});
            var Q3;
            {var subQ0=sQuery(id+"F4.wireOp",EDGE,"E30");Q3=makeQuery(id+"F8.boolean.opBoolean","SPLIT",EDGE,{"disambiguationData":[TD([makeQuery(id+"F5.opExtrude","SWEPT_FACE",FACE,{"disambiguationData":[OSD([sQuery(id+"F4.wireOp",EDGE,"E35.filletArc")])]})])],"derivedFrom":makeQuery(id+"F5.opExtrude","CAP_EDGE",EDGE,{"disambiguationData":[OSD([subQ0])],"isStart":false})});}
            var Q4;
            {var subQ0=sQuery(id+"F0.wireOp",EDGE,"E25.7");var subQ1=sQuery(id+"F0.wireOp",EDGE,"E25.1");var subQ2=sQuery(id+"F0.wireOp",EDGE,"E25.6");var subQ3=sQuery(id+"F0.wireOp",EDGE,"E25.5");var subQ4=sQuery(id+"F0.wireOp",EDGE,"E25.4");var subQ5=sQuery(id+"F0.wireOp",EDGE,"E25.0");var subQ6=sQuery(id+"F0.wireOp",EDGE,"E25.2");var subQ7=sQuery(id+"F0.wireOp",EDGE,"E25.3");Q4=makeQuery(id+"F8.boolean.opBoolean","INTERSECT",EDGE,{"derivedFrom":[makeQuery(id+"F5.boolean.opBoolean","SPLIT",FACE,{"disambiguationData":[TD([makeQuery(id+"F2.opExtrude","SWEPT_FACE",FACE,{"disambiguationData":[OSD([subQ5])]})])],"derivedFrom":makeQuery(id+"F3.boolean.opBoolean","COPY",FACE,{"derivedFrom":makeQuery(id+"F3.opExtrude","CAP_FACE",FACE,{"disambiguationData":[OSD([subQ5,subQ1,subQ6,subQ7,subQ4,subQ3,subQ2,subQ0])],"isStart":false})})}),makeQuery(id+"F8.opExtrude","SWEPT_FACE",FACE,{"disambiguationData":[OSD([sQuery(id+"F7.wireOp",EDGE,"E67")])]})]});}
            var Q5;
            Q5=makeQuery(id+"F8.boolean.opBoolean","INTERSECT",EDGE,{"disambiguationData":[OD(0.0)],"derivedFrom":[makeQuery(id+"F5.opExtrude","SWEPT_FACE",FACE,{"disambiguationData":[OSD([sQuery(id+"F4.wireOp",EDGE,"E30")])]}),makeQuery(id+"F8.opExtrude","SWEPT_FACE",FACE,{"disambiguationData":[OSD([sQuery(id+"F7.wireOp",EDGE,"E67")])]})]});
            fillet(context, id + "F14", {"entities" : qUnion([Q0, Q1, Q2, Q3, Q4, Q5]), "radius" : 3 * mm, "tangentPropagation" : true, "allowEdgeOverflow" : false});
        }
        {
            var Q0;
            Q0=makeQuery(id+"F1.opExtrude","CAP_EDGE",EDGE,{"disambiguationData":[OSD([sQuery(id+"F0.wireOp",EDGE,"E1.bottom")])],"isStart":false});
            fillet(context, id + "F15", {"entities" : qUnion([Q0]), "radius" : 2 * mm, "tangentPropagation" : true, "allowEdgeOverflow" : false});
        }
        {
            var Q0;
            {var subQ0=sQuery(id+"F0.wireOp",EDGE,"E22.filletArc");var subQ1=sQuery(id+"F0.wireOp",EDGE,"E7");var subQ2=sQuery(id+"F0.wireOp",EDGE,"E6");var subQ3=sQuery(id+"F0.wireOp",EDGE,"E5");var subQ4=sQuery(id+"F0.wireOp",EDGE,"E4");var subQ5=sQuery(id+"F0.wireOp",EDGE,"E1.bottom");var subQ6=sQuery(id+"F0.wireOp",EDGE,"E21.filletArc");var subQ7=sQuery(id+"F0.wireOp",EDGE,"E1.top");var subQ8=sQuery(id+"F0.wireOp",EDGE,"E1.left");var subQ9=sQuery(id+"F0.wireOp",EDGE,"E1.right");var subQ10=sQuery(id+"F0.wireOp",EDGE,"E23.filletArc");var subQ11=sQuery(id+"F0.wireOp",EDGE,"E24.filletArc");Q0=makeQuery(id+"F2.boolean.opBoolean","SPLIT",FACE,{"disambiguationData":[TD([makeQuery(id+"F1.opExtrude","SWEPT_FACE",FACE,{"disambiguationData":[OSD([subQ5])]})])],"derivedFrom":makeQuery(id+"F1.opExtrude","CAP_FACE",FACE,{"disambiguationData":[OSD([subQ5,subQ7,subQ8,subQ9,subQ4,subQ3,subQ2,subQ1,subQ6,subQ0,subQ10,subQ11])],"isStart":true})});}
            var sketch = newSketch(context, id + "F16", { "sketchPlane" : qUnion([Q0])});
            skLineSegment(sketch, "E79", {"start": v(33.4, 74.25) * mm, "end": v(15.4, 92.25) * mm});
            skLineSegment(sketch, "E80", {"start": v(15.4, 92.25) * mm, "end": v(15.4, 104.25) * mm});
            skArc(sketch, "E81", {"start": v(15.4, 104.25) * mm, "mid": v(0.4, 119.25) * mm, "end": v(-14.6, 104.25) * mm});
            skLineSegment(sketch, "E82", {"start": v(-14.6, 104.25) * mm, "end": v(-14.6, 92.25) * mm});
            skLineSegment(sketch, "E83", {"start": v(-14.6, 92.25) * mm, "end": v(-32.56, 74.25) * mm});
            skCircle(sketch, "E84", {"center": v(0.4, 104.25) * mm, "radius": 6 * mm});
            skLineSegment(sketch, "E85.MirrorCS", {"start": v(-14.6, -92.25) * mm, "end": v(-32.56, -74.25) * mm});
            skLineSegment(sketch, "E86.MirrorCS", {"start": v(-14.6, -104.25) * mm, "end": v(-14.6, -92.25) * mm});
            skArc(sketch, "E87.MirrorCS", {"start": v(15.4, -104.25) * mm, "mid": v(0.4, -119.25) * mm, "end": v(-14.6, -104.25) * mm});
            skLineSegment(sketch, "E88.MirrorCS", {"start": v(15.4, -92.25) * mm, "end": v(15.4, -104.25) * mm});
            skLineSegment(sketch, "E89.MirrorCS", {"start": v(33.4, -74.25) * mm, "end": v(15.4, -92.25) * mm});
            skCircle(sketch, "E90.MirrorC", {"center": v(0.4, -104.25) * mm, "radius": 6 * mm});
            skSolve(sketch);
        }
        {
            var Q0;
            Q0=makeQuery(id+"F16.imprint","IMPRINT",FACE,{"disambiguationData":[TD([[makeQuery(id+"F16.imprint","IMPRINT",EDGE,{"derivedFrom":makeQuery(id+"F1.opExtrude","CAP_EDGE",EDGE,{"disambiguationData":[OSD([sQuery(id+"F0.wireOp",EDGE,"E1.left")])],"isStart":true})}),-1.0]])]});
            var Q1;
            {var subQ0=sQuery(id+"F16.wireOp",EDGE,"E85.MirrorCS");Q1=makeQuery(id+"F16.imprint","IMPRINT",FACE,{"disambiguationData":[TD([[makeQuery(id+"F16.imprint","IMPRINT",EDGE,{"derivedFrom":subQ0}),-1.0]])]});}
            var Q2;
            {var subQ0=sQuery(id+"F16.wireOp",EDGE,"E79");Q2=makeQuery(id+"F16.imprint","IMPRINT",FACE,{"disambiguationData":[TD([[makeQuery(id+"F16.imprint","IMPRINT",EDGE,{"derivedFrom":subQ0}),1.0]])]});}
            var Q3;
            Q3=makeQuery(id+"F2.opExtrude","CAP_FACE",FACE,{"disambiguationData":[OSD([sQuery(id+"F0.wireOp",EDGE,"E12"),sQuery(id+"F0.wireOp",EDGE,"E13"),sQuery(id+"F0.wireOp",EDGE,"E14"),sQuery(id+"F0.wireOp",EDGE,"E15"),sQuery(id+"F0.wireOp",EDGE,"E17.filletArc"),sQuery(id+"F0.wireOp",EDGE,"E18.filletArc"),sQuery(id+"F0.wireOp",EDGE,"E19.filletArc"),sQuery(id+"F0.wireOp",EDGE,"E20.filletArc"),sQuery(id+"F0.wireOp",EDGE,"E25.0"),sQuery(id+"F0.wireOp",EDGE,"E25.1"),sQuery(id+"F0.wireOp",EDGE,"E25.2"),sQuery(id+"F0.wireOp",EDGE,"E25.3"),sQuery(id+"F0.wireOp",EDGE,"E25.4"),sQuery(id+"F0.wireOp",EDGE,"E25.5"),sQuery(id+"F0.wireOp",EDGE,"E25.6"),sQuery(id+"F0.wireOp",EDGE,"E25.7")])],"isStart":false});
            extrude(context, id + "F17", {"entities" : qUnion([Q0, Q1, Q2]), "operationType" : NewBodyOperationType.ADD, "endBound" : BoundingType.UP_TO_SURFACE, "endBoundEntityFace" : qUnion([Q3]), "depth" : 25 * mm});
        }
    });
